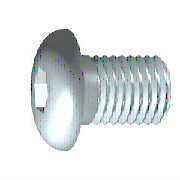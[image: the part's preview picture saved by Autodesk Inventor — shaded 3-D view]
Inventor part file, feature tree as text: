
AUTODESK INVENTOR PART (.ipt)
format: ipt  version: 2013 (Build 170138000, 138)  size: 191,488 bytes
history: native  units: mm (DEFAULTED — no unit token found)
features: sketch x2, extrude x1, plane x1
ambient origin geometry x7: Origin, YZ Plane, XY Plane, X Axis, Y Axis, Z Axis, Center Point
bodies: Solid1 (feature_tree), Body (feature_tree)
feature tree (4):
  extrude  "Slot"  Depth=0.306725mm
  plane  "Work Plane1"
  sketch  "Sketch1"  dims[d0=11.0mm d1=0.306725mm]
  sketch  "Sketch2"  dims[d2=1.65mm d3=1.04mm d4=60.0deg d5=3.0mm d6=3.0mm d7=2.309401mm d8=5.7mm d10=90.0deg d11=10.0mm d9=0.0mm d12=11.0mm d13=0.0mm d14=0.306725mm d15=0.306725mm d16=1.425mm d17=0.0mm d18=0.0mm d19=12.0mm d27=45.0deg d28=0.1mm d29=0.1mm]
